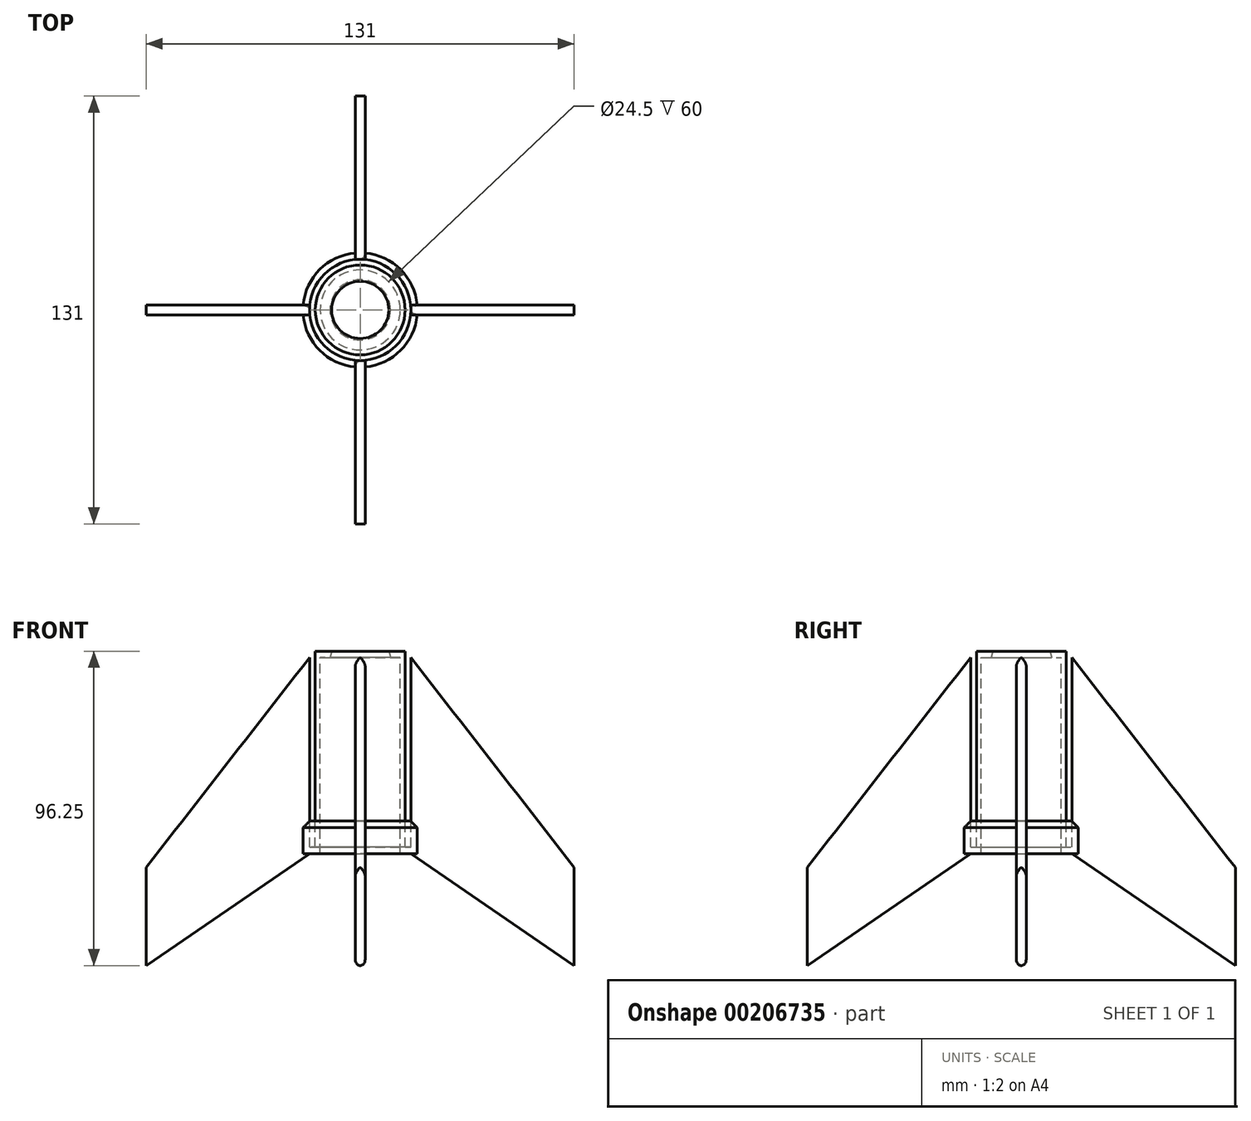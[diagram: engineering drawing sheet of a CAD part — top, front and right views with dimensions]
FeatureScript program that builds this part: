
annotation { "Feature Type Name" : "Feature", "Feature Type Description" : "" }
export const myFeature = defineFeature(function(context is Context, id is Id, definition is map)
    precondition{}
    {
        {
            var Q0;
            Q0=qCreatedBy(makeId("Right.planeOp"),FACE);
            var sketch = newSketch(context, id + "F0", { "sketchPlane" : qUnion([Q0])});
            skLineSegment(sketch, "E0", {"start": v(-8.75, 52) * mm, "end": v(-13.75, 52) * mm});
            skLineSegment(sketch, "E1", {"start": v(-13.75, 52) * mm, "end": v(-13.75, -8) * mm});
            skLineSegment(sketch, "E2", {"start": v(-13.75, -8) * mm, "end": v(-15.5, -8) * mm});
            skLineSegment(sketch, "E3", {"start": v(-15.5, -8) * mm, "end": v(-15.5, 0) * mm});
            skLineSegment(sketch, "E4", {"start": v(-15.5, 0) * mm, "end": v(-17.5, 0) * mm});
            skLineSegment(sketch, "E5", {"start": v(-17.5, 0) * mm, "end": v(-17.5, -10) * mm});
            skLineSegment(sketch, "E6", {"start": v(-17.5, -10) * mm, "end": v(-12.25, -10) * mm});
            skLineSegment(sketch, "E7", {"start": v(-12.25, -10) * mm, "end": v(-12.25, 50) * mm});
            skLineSegment(sketch, "E8", {"start": v(-12.25, 50) * mm, "end": v(-9.25, 50) * mm});
            skLineSegment(sketch, "E9", {"start": v(-8.75, 52) * mm, "end": v(-9.25, 50) * mm});
            skPoint(sketch, "E10.orphan", {"position": v(-14.72, 28.11) * mm});
            skPoint(sketch, "E11.orphan", {"position": v(-14.72, 50) * mm});
            skSolve(sketch);
        }
        {
            var Q0;
            Q0=qCreatedBy(makeId("Right.planeOp"),FACE);
            var sketch = newSketch(context, id + "F1", { "sketchPlane" : qUnion([Q0])});
            skLineSegment(sketch, "E12", {"start": v(0, 50.87) * mm, "end": v(0, -29.55) * mm, "construction": true});
            skSolve(sketch);
        }
        {
            var Q0;
            Q0=qSketchRegion(id+"F0",true);
            var Q1;
            Q1=sQuery(id+"F1.wireOp",EDGE,"E12");
            revolve(context, id + "F2", {"entities" : qUnion([Q0]), "axis" : qUnion([Q1]), "revolveType" : RevolveType.FULL});
        }
        {
            var Q0;
            Q0=qCreatedBy(makeId("Right.planeOp"),FACE);
            var sketch = newSketch(context, id + "F3", { "sketchPlane" : qUnion([Q0])});
            skLineSegment(sketch, "E13", {"start": v(-17.5, -10) * mm, "end": v(-15.5, -10) * mm});
            skLineSegment(sketch, "E14", {"start": v(-15.5, -10) * mm, "end": v(-65.5, -44.25) * mm});
            skLineSegment(sketch, "E15", {"start": v(-65.5, -44.25) * mm, "end": v(-65.5, -14.25) * mm});
            skLineSegment(sketch, "E16", {"start": v(-15.5, -10) * mm, "end": v(-15.5, 50) * mm});
            skLineSegment(sketch, "E17", {"start": v(-15.5, 50) * mm, "end": v(-65.5, -14.25) * mm});
            skLineSegment(sketch, "E18", {"start": v(-17.5, -10) * mm, "end": v(-68.6, -10) * mm});
            skSolve(sketch);
        }
        {
            var Q0;
            Q0=qSketchRegion(id+"F3",true);
            extrude(context, id + "F4", {"entities" : qUnion([Q0]), "operationType" : NewBodyOperationType.ADD, "endBound" : BoundingType.SYMMETRIC, "depth" : 3 * mm});
        }
        {
            var Q0;
            Q0=makeQuery(id+"F2.opRevolve","SWEPT_BODY",BODY,{"disambiguationData":[OSD([sQuery(id+"F0.wireOp",EDGE,"E0"),sQuery(id+"F0.wireOp",EDGE,"E1"),sQuery(id+"F0.wireOp",EDGE,"E2"),sQuery(id+"F0.wireOp",EDGE,"E3"),sQuery(id+"F0.wireOp",EDGE,"E4"),sQuery(id+"F0.wireOp",EDGE,"E5"),sQuery(id+"F0.wireOp",EDGE,"E6"),sQuery(id+"F0.wireOp",EDGE,"E7"),sQuery(id+"F0.wireOp",EDGE,"E8"),sQuery(id+"F0.wireOp",EDGE,"E9")])]});
            var Q1;
            Q1=sQuery(id+"F1.wireOp",EDGE,"E12");
            circularPattern(context, id + "F5", {"entities" : qUnion([Q0]), "axis" : qUnion([Q1]), "angle" : 360 * degree, "instanceCount" : 4, "equalSpace" : true});
        }
        {
            var Q0;
            Q0=makeQuery(id+"F5.opPattern","COPY",BODY,{"derivedFrom":makeQuery(id+"F2.opRevolve","SWEPT_BODY",BODY,{"disambiguationData":[OSD([sQuery(id+"F0.wireOp",EDGE,"E0"),sQuery(id+"F0.wireOp",EDGE,"E1"),sQuery(id+"F0.wireOp",EDGE,"E2"),sQuery(id+"F0.wireOp",EDGE,"E3"),sQuery(id+"F0.wireOp",EDGE,"E4"),sQuery(id+"F0.wireOp",EDGE,"E5"),sQuery(id+"F0.wireOp",EDGE,"E6"),sQuery(id+"F0.wireOp",EDGE,"E7"),sQuery(id+"F0.wireOp",EDGE,"E8"),sQuery(id+"F0.wireOp",EDGE,"E9")])]}),"instanceName":"1"});
            var Q1;
            Q1=makeQuery(id+"F5.opPattern","COPY",BODY,{"derivedFrom":makeQuery(id+"F2.opRevolve","SWEPT_BODY",BODY,{"disambiguationData":[OSD([sQuery(id+"F0.wireOp",EDGE,"E0"),sQuery(id+"F0.wireOp",EDGE,"E1"),sQuery(id+"F0.wireOp",EDGE,"E2"),sQuery(id+"F0.wireOp",EDGE,"E3"),sQuery(id+"F0.wireOp",EDGE,"E4"),sQuery(id+"F0.wireOp",EDGE,"E5"),sQuery(id+"F0.wireOp",EDGE,"E6"),sQuery(id+"F0.wireOp",EDGE,"E7"),sQuery(id+"F0.wireOp",EDGE,"E8"),sQuery(id+"F0.wireOp",EDGE,"E9")])]}),"instanceName":"3"});
            var Q2;
            Q2=makeQuery(id+"F5.opPattern","COPY",BODY,{"derivedFrom":makeQuery(id+"F2.opRevolve","SWEPT_BODY",BODY,{"disambiguationData":[OSD([sQuery(id+"F0.wireOp",EDGE,"E0"),sQuery(id+"F0.wireOp",EDGE,"E1"),sQuery(id+"F0.wireOp",EDGE,"E2"),sQuery(id+"F0.wireOp",EDGE,"E3"),sQuery(id+"F0.wireOp",EDGE,"E4"),sQuery(id+"F0.wireOp",EDGE,"E5"),sQuery(id+"F0.wireOp",EDGE,"E6"),sQuery(id+"F0.wireOp",EDGE,"E7"),sQuery(id+"F0.wireOp",EDGE,"E8"),sQuery(id+"F0.wireOp",EDGE,"E9")])]}),"instanceName":"2"});
            var Q3;
            Q3=makeQuery(id+"F2.opRevolve","SWEPT_BODY",BODY,{"disambiguationData":[OSD([sQuery(id+"F0.wireOp",EDGE,"E0"),sQuery(id+"F0.wireOp",EDGE,"E1"),sQuery(id+"F0.wireOp",EDGE,"E2"),sQuery(id+"F0.wireOp",EDGE,"E3"),sQuery(id+"F0.wireOp",EDGE,"E4"),sQuery(id+"F0.wireOp",EDGE,"E5"),sQuery(id+"F0.wireOp",EDGE,"E6"),sQuery(id+"F0.wireOp",EDGE,"E7"),sQuery(id+"F0.wireOp",EDGE,"E8"),sQuery(id+"F0.wireOp",EDGE,"E9")])]});
            booleanBodies(context, id + "F6", {"operationType" : BooleanOperationType.UNION, "tools" : qUnion([Q0, Q1, Q2, Q3])});
        }
        {
            var Q0;
            Q0=makeQuery(id+"F4.opExtrude","CAP_EDGE",EDGE,{"disambiguationData":[OSD([sQuery(id+"F3.wireOp",EDGE,"E17")])],"isStart":false});
            var Q1;
            Q1=makeQuery(id+"F5.opPattern","COPY",EDGE,{"derivedFrom":makeQuery(id+"F4.opExtrude","CAP_EDGE",EDGE,{"disambiguationData":[OSD([sQuery(id+"F3.wireOp",EDGE,"E17")])],"isStart":false}),"instanceName":"3"});
            var Q2;
            Q2=makeQuery(id+"F5.opPattern","COPY",EDGE,{"derivedFrom":makeQuery(id+"F4.opExtrude","CAP_EDGE",EDGE,{"disambiguationData":[OSD([sQuery(id+"F3.wireOp",EDGE,"E17")])],"isStart":true}),"instanceName":"3"});
            var Q3;
            Q3=makeQuery(id+"F5.opPattern","COPY",EDGE,{"derivedFrom":makeQuery(id+"F4.opExtrude","CAP_EDGE",EDGE,{"disambiguationData":[OSD([sQuery(id+"F3.wireOp",EDGE,"E17")])],"isStart":true}),"instanceName":"2"});
            var Q4;
            Q4=makeQuery(id+"F5.opPattern","COPY",EDGE,{"derivedFrom":makeQuery(id+"F4.opExtrude","CAP_EDGE",EDGE,{"disambiguationData":[OSD([sQuery(id+"F3.wireOp",EDGE,"E17")])],"isStart":false}),"instanceName":"2"});
            var Q5;
            Q5=makeQuery(id+"F5.opPattern","COPY",EDGE,{"derivedFrom":makeQuery(id+"F4.opExtrude","CAP_EDGE",EDGE,{"disambiguationData":[OSD([sQuery(id+"F3.wireOp",EDGE,"E17")])],"isStart":true}),"instanceName":"1"});
            var Q6;
            Q6=makeQuery(id+"F5.opPattern","COPY",EDGE,{"derivedFrom":makeQuery(id+"F4.opExtrude","CAP_EDGE",EDGE,{"disambiguationData":[OSD([sQuery(id+"F3.wireOp",EDGE,"E17")])],"isStart":false}),"instanceName":"1"});
            var Q7;
            Q7=makeQuery(id+"F4.opExtrude","CAP_EDGE",EDGE,{"disambiguationData":[OSD([sQuery(id+"F3.wireOp",EDGE,"E17")])],"isStart":true});
            fillet(context, id + "F7", {"entities" : qUnion([Q0, Q1, Q2, Q3, Q4, Q5, Q6, Q7]), "radius" : 1.5 * mm, "tangentPropagation" : true, "rho" : .2, "crossSection" : FilletCrossSection.CONIC, "allowEdgeOverflow" : false});
        }
        {
            var Q0;
            Q0=makeQuery(id+"F5.opPattern","COPY",EDGE,{"derivedFrom":makeQuery(id+"F4.opExtrude","CAP_EDGE",EDGE,{"disambiguationData":[OSD([sQuery(id+"F3.wireOp",EDGE,"E14")])],"isStart":false}),"instanceName":"1"});
            var Q1;
            Q1=makeQuery(id+"F5.opPattern","COPY",EDGE,{"derivedFrom":makeQuery(id+"F4.opExtrude","CAP_EDGE",EDGE,{"disambiguationData":[OSD([sQuery(id+"F3.wireOp",EDGE,"E14")])],"isStart":true}),"instanceName":"1"});
            var Q2;
            Q2=makeQuery(id+"F5.opPattern","COPY",EDGE,{"derivedFrom":makeQuery(id+"F4.opExtrude","CAP_EDGE",EDGE,{"disambiguationData":[OSD([sQuery(id+"F3.wireOp",EDGE,"E14")])],"isStart":false}),"instanceName":"2"});
            var Q3;
            Q3=makeQuery(id+"F5.opPattern","COPY",EDGE,{"derivedFrom":makeQuery(id+"F4.opExtrude","CAP_EDGE",EDGE,{"disambiguationData":[OSD([sQuery(id+"F3.wireOp",EDGE,"E14")])],"isStart":true}),"instanceName":"2"});
            var Q4;
            Q4=makeQuery(id+"F5.opPattern","COPY",EDGE,{"derivedFrom":makeQuery(id+"F4.opExtrude","CAP_EDGE",EDGE,{"disambiguationData":[OSD([sQuery(id+"F3.wireOp",EDGE,"E14")])],"isStart":false}),"instanceName":"3"});
            var Q5;
            Q5=makeQuery(id+"F5.opPattern","COPY",EDGE,{"derivedFrom":makeQuery(id+"F4.opExtrude","CAP_EDGE",EDGE,{"disambiguationData":[OSD([sQuery(id+"F3.wireOp",EDGE,"E14")])],"isStart":true}),"instanceName":"3"});
            var Q6;
            Q6=makeQuery(id+"F4.opExtrude","CAP_EDGE",EDGE,{"disambiguationData":[OSD([sQuery(id+"F3.wireOp",EDGE,"E14")])],"isStart":false});
            var Q7;
            Q7=makeQuery(id+"F4.opExtrude","CAP_EDGE",EDGE,{"disambiguationData":[OSD([sQuery(id+"F3.wireOp",EDGE,"E14")])],"isStart":true});
            fillet(context, id + "F8", {"entities" : qUnion([Q0, Q1, Q2, Q3, Q4, Q5, Q6, Q7]), "radius" : 1.5 * mm, "tangentPropagation" : true, "allowEdgeOverflow" : false});
        }
        {
            var Q0;
            {var subQ0=sQuery(id+"F3.wireOp",EDGE,"E17");var subQ1=sQuery(id+"F3.wireOp",EDGE,"E16");var subQ2=sQuery(id+"F3.wireOp",EDGE,"E15");var subQ3=sQuery(id+"F3.wireOp",EDGE,"E14");var subQ4=sQuery(id+"F0.wireOp",EDGE,"E4");var subQ5=sQuery(id+"F0.wireOp",EDGE,"E5");Q0=makeQuery(id+"F6.opBoolean","SPLIT",EDGE,{"disambiguationData":[TD([makeQuery(id+"F4.opExtrude","CAP_FACE",FACE,{"disambiguationData":[OSD([subQ3,subQ2,subQ1,subQ0])],"isStart":false})])],"derivedFrom":makeQuery(id+"F5.opPattern","COPY",EDGE,{"derivedFrom":makeQuery(id+"F2.opRevolve","SWEPT_EDGE",EDGE,{"disambiguationData":[OSD([subQ4,subQ5])]}),"instanceName":"1"})});}
            var Q1;
            {var subQ0=sQuery(id+"F0.wireOp",EDGE,"E4");var subQ1=sQuery(id+"F0.wireOp",EDGE,"E5");var subQ2=sQuery(id+"F3.wireOp",EDGE,"E17");var subQ3=sQuery(id+"F3.wireOp",EDGE,"E16");var subQ4=sQuery(id+"F3.wireOp",EDGE,"E15");var subQ5=sQuery(id+"F3.wireOp",EDGE,"E14");Q1=makeQuery(id+"F6.opBoolean","SPLIT",EDGE,{"disambiguationData":[TD([makeQuery(id+"F5.opPattern","COPY",FACE,{"derivedFrom":makeQuery(id+"F4.opExtrude","CAP_FACE",FACE,{"disambiguationData":[OSD([subQ5,subQ4,subQ3,subQ2])],"isStart":true}),"instanceName":"2"})])],"derivedFrom":makeQuery(id+"F5.opPattern","COPY",EDGE,{"derivedFrom":makeQuery(id+"F2.opRevolve","SWEPT_EDGE",EDGE,{"disambiguationData":[OSD([subQ0,subQ1])]}),"instanceName":"1"})});}
            var Q2;
            {var subQ0=sQuery(id+"F0.wireOp",EDGE,"E4");var subQ1=sQuery(id+"F0.wireOp",EDGE,"E5");var subQ2=sQuery(id+"F3.wireOp",EDGE,"E17");var subQ3=sQuery(id+"F3.wireOp",EDGE,"E16");var subQ4=sQuery(id+"F3.wireOp",EDGE,"E15");var subQ5=sQuery(id+"F3.wireOp",EDGE,"E14");Q2=makeQuery(id+"F6.opBoolean","SPLIT",EDGE,{"disambiguationData":[TD([makeQuery(id+"F5.opPattern","COPY",FACE,{"derivedFrom":makeQuery(id+"F4.opExtrude","CAP_FACE",FACE,{"disambiguationData":[OSD([subQ5,subQ4,subQ3,subQ2])],"isStart":true}),"instanceName":"1"})])],"derivedFrom":makeQuery(id+"F5.opPattern","COPY",EDGE,{"derivedFrom":makeQuery(id+"F2.opRevolve","SWEPT_EDGE",EDGE,{"disambiguationData":[OSD([subQ0,subQ1])]}),"instanceName":"1"})});}
            var Q3;
            {var subQ0=sQuery(id+"F3.wireOp",EDGE,"E17");var subQ1=sQuery(id+"F3.wireOp",EDGE,"E16");var subQ2=sQuery(id+"F3.wireOp",EDGE,"E15");var subQ3=sQuery(id+"F3.wireOp",EDGE,"E14");var subQ4=sQuery(id+"F0.wireOp",EDGE,"E4");var subQ5=sQuery(id+"F0.wireOp",EDGE,"E5");Q3=makeQuery(id+"F6.opBoolean","SPLIT",EDGE,{"disambiguationData":[TD([makeQuery(id+"F4.opExtrude","CAP_FACE",FACE,{"disambiguationData":[OSD([subQ3,subQ2,subQ1,subQ0])],"isStart":true})])],"derivedFrom":makeQuery(id+"F5.opPattern","COPY",EDGE,{"derivedFrom":makeQuery(id+"F2.opRevolve","SWEPT_EDGE",EDGE,{"disambiguationData":[OSD([subQ4,subQ5])]}),"instanceName":"1"})});}
            chamfer(context, id + "F9", {"entities" : qUnion([Q0, Q1, Q2, Q3]), "width" : 2 * mm, "tangentPropagation" : true});
        }
    });
